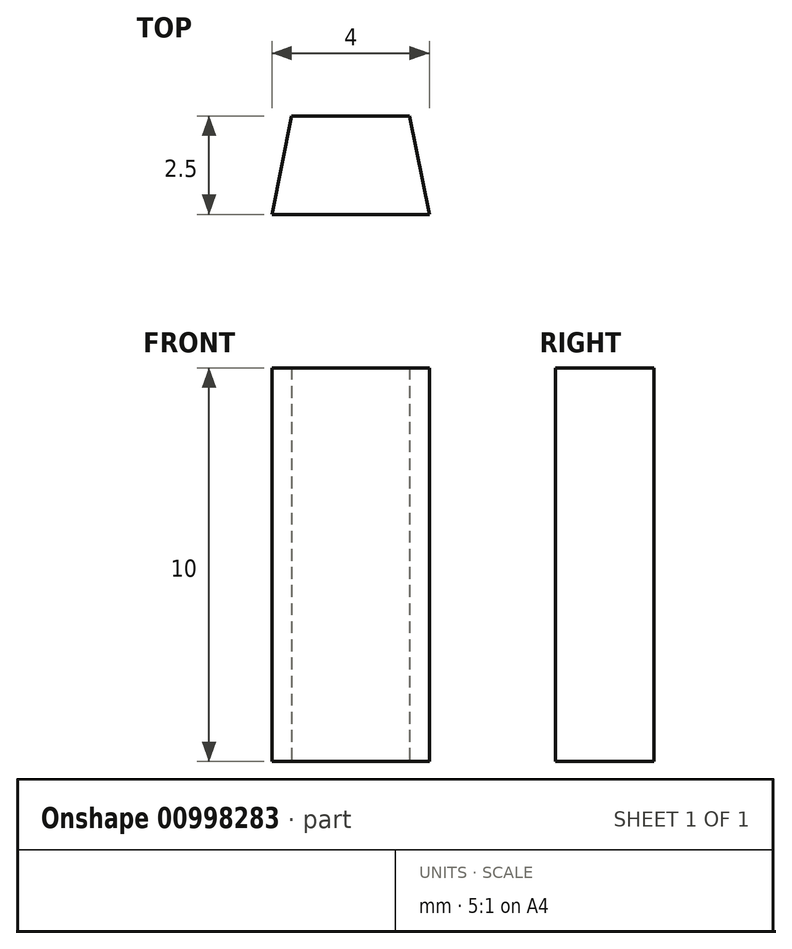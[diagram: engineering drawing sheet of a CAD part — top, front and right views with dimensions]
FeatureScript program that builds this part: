
annotation { "Feature Type Name" : "Feature", "Feature Type Description" : "" }
export const myFeature = defineFeature(function(context is Context, id is Id, definition is map)
    precondition{}
    {
        {
            var Q0;
            Q0=qCreatedBy(makeId("Top.planeOp"),FACE);
            var sketch = newSketch(context, id + "F0", { "sketchPlane" : qUnion([Q0])});
            skLineSegment(sketch, "E0", {"start": v(-1.34, 3.23) * mm, "end": v(-1.84, 0.73) * mm});
            skLineSegment(sketch, "E1", {"start": v(1.66, 3.23) * mm, "end": v(2.16, 0.73) * mm});
            skLineSegment(sketch, "E2", {"start": v(-1.84, 0.73) * mm, "end": v(2.16, 0.73) * mm});
            skLineSegment(sketch, "E3", {"start": v(-1.34, 3.23) * mm, "end": v(1.66, 3.23) * mm});
            skSolve(sketch);
        }
        {
            var Q0;
            Q0=makeQuery(id+"F0.imprint","IMPRINT",FACE,{"disambiguationData":[TD([[makeQuery(id+"F0.imprint","IMPRINT",EDGE,{"derivedFrom":sQuery(id+"F0.wireOp",EDGE,"E0")}),1.0]])]});
            extrude(context, id + "F1", {"entities" : qUnion([Q0]), "depth" : 10 * mm, "offsetDistance" : 25 * mm});
        }
    });
